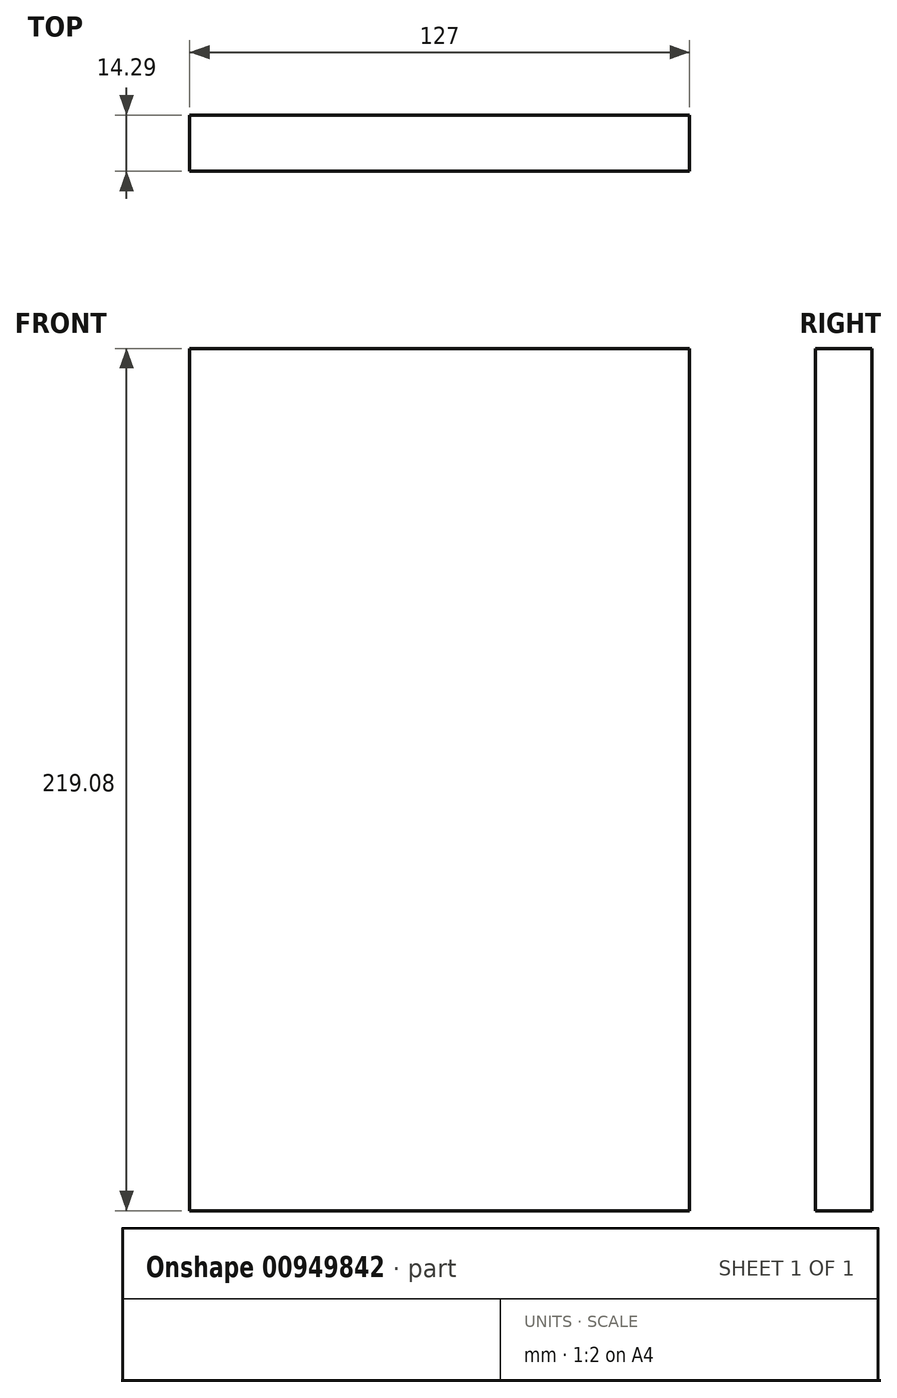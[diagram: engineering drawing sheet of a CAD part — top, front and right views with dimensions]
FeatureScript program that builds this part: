
annotation { "Feature Type Name" : "Feature", "Feature Type Description" : "" }
export const myFeature = defineFeature(function(context is Context, id is Id, definition is map)
    precondition{}
    {
        {
            var Q0;
            Q0=qCreatedBy(makeId("Front.planeOp"),FACE);
            var sketch = newSketch(context, id + "F0", { "sketchPlane" : qUnion([Q0])});
            skLineSegment(sketch, "E0.bottom", {"start": v(-63.5, 109.54) * mm, "end": v(63.5, 109.54) * mm});
            skLineSegment(sketch, "E0.top", {"start": v(-63.5, -109.54) * mm, "end": v(63.5, -109.54) * mm});
            skLineSegment(sketch, "E0.left", {"start": v(-63.5, 109.54) * mm, "end": v(-63.5, -109.54) * mm});
            skLineSegment(sketch, "E0.right", {"start": v(63.5, 109.54) * mm, "end": v(63.5, -109.54) * mm});
            skLineSegment(sketch, "E1", {"start": v(0, 109.54) * mm, "end": v(0, -109.54) * mm, "construction": true});
            skLineSegment(sketch, "E2", {"start": v(-63.5, 0) * mm, "end": v(63.5, 0) * mm, "construction": true});
            skSolve(sketch);
        }
        {
            var Q0;
            Q0=qSketchRegion(id+"F0",true);
            extrude(context, id + "F1", {"entities" : qUnion([Q0]), "depth" : 14.29 * mm, "offsetDistance" : 25.4 * mm});
        }
    });
